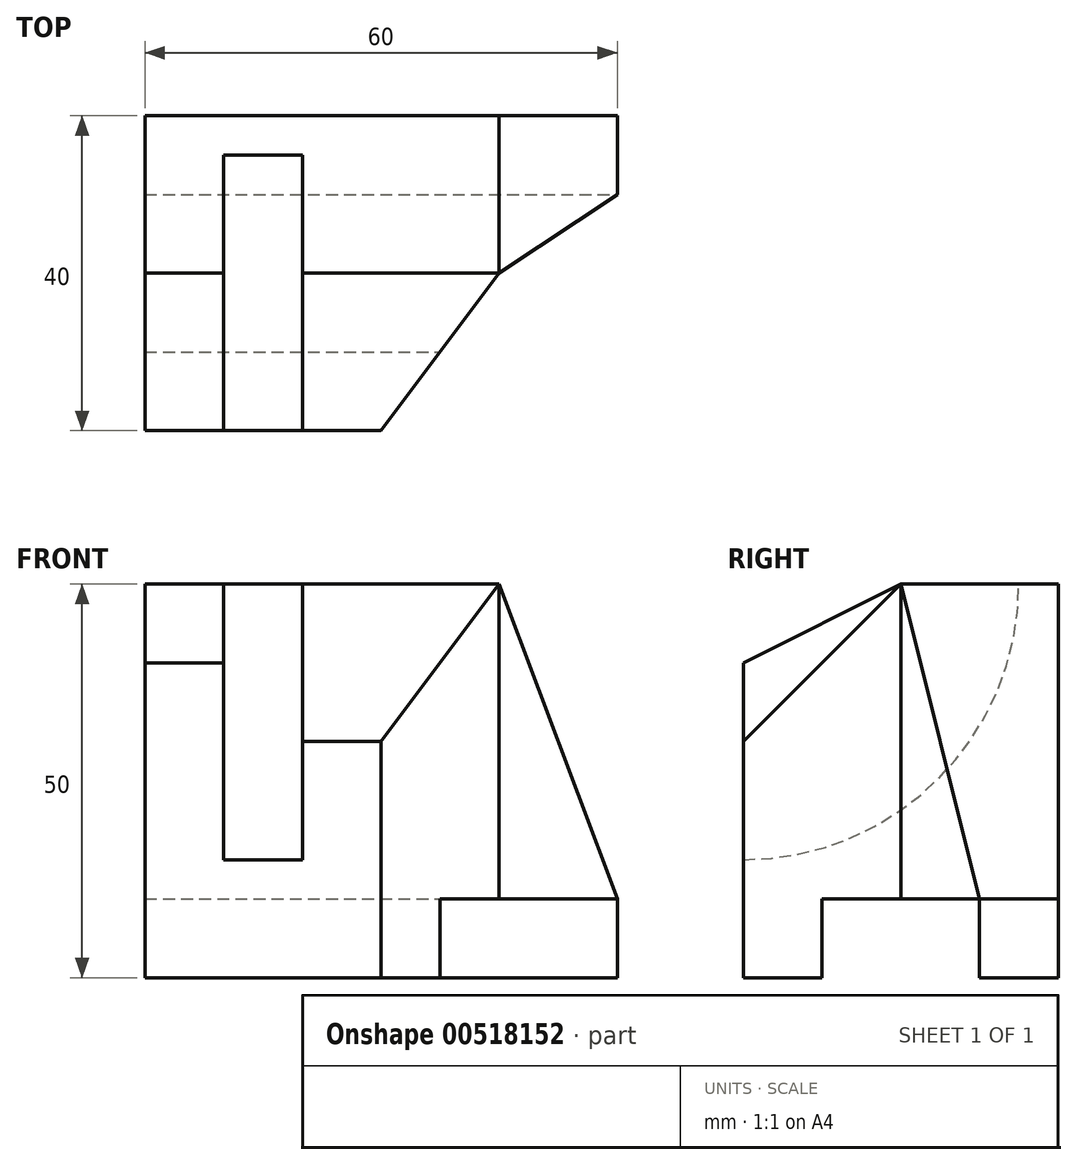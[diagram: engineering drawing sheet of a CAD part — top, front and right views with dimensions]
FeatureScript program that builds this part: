
annotation { "Feature Type Name" : "Feature", "Feature Type Description" : "" }
export const myFeature = defineFeature(function(context is Context, id is Id, definition is map)
    precondition{}
    {
        {
            var Q0;
            Q0=qCreatedBy(makeId("Top.planeOp"),FACE);
            var sketch = newSketch(context, id + "F0", { "sketchPlane" : qUnion([Q0])});
            skLineSegment(sketch, "E0.bottom", {"start": v(0, 0) * mm, "end": v(60, 0) * mm});
            skLineSegment(sketch, "E0.top", {"start": v(0, 40) * mm, "end": v(60, 40) * mm});
            skLineSegment(sketch, "E0.left", {"start": v(0, 0) * mm, "end": v(0, 40) * mm});
            skLineSegment(sketch, "E0.right", {"start": v(60, 0) * mm, "end": v(60, 40) * mm});
            skSolve(sketch);
        }
        {
            var Q0;
            Q0 = qSketchRegion(id + "F0", true);
            extrude(context, id + "F1", {"entities" : qUnion([Q0]), "depth" : 50 * mm, "offsetDistance" : 25 * mm});
        }
        {
            var Q0;
            Q0=makeQuery(id+"F1.opExtrude","SWEPT_FACE",FACE,{"disambiguationData":[OSD([sQuery(id+"F0.wireOp",EDGE,"E0.right")])]});
            var sketch = newSketch(context, id + "F2", { "sketchPlane" : qUnion([Q0])});
            skLineSegment(sketch, "E1.bottom", {"start": v(10, 0) * mm, "end": v(30, 0) * mm});
            skLineSegment(sketch, "E1.top", {"start": v(10, 10) * mm, "end": v(30, 10) * mm});
            skLineSegment(sketch, "E1.left", {"start": v(10, 0) * mm, "end": v(10, 10) * mm});
            skLineSegment(sketch, "E1.right", {"start": v(30, 0) * mm, "end": v(30, 10) * mm});
            skSolve(sketch);
        }
        {
            var Q0;
            Q0=makeQuery(id+"F2.imprint","IMPRINT",FACE,{"disambiguationData":[TD([[makeQuery(id+"F2.imprint","IMPRINT",EDGE,{"derivedFrom":sQuery(id+"F2.wireOp",EDGE,"E1.bottom")}),1.0]])]});
            extrude(context, id + "F3", {"entities" : qUnion([Q0]), "operationType" : NewBodyOperationType.REMOVE, "endBound" : BoundingType.THROUGH_ALL, "oppositeDirection" : true, "depth" : 25 * mm, "offsetDistance" : 25 * mm});
        }
        {
            var Q0;
            Q0=makeQuery(id+"F1.opExtrude","CAP_FACE",FACE,{"disambiguationData":[OSD([sQuery(id+"F0.wireOp",EDGE,"E0.bottom"),sQuery(id+"F0.wireOp",EDGE,"E0.top"),sQuery(id+"F0.wireOp",EDGE,"E0.left"),sQuery(id+"F0.wireOp",EDGE,"E0.right")])],"isStart":false});
            var sketch = newSketch(context, id + "F4", { "sketchPlane" : qUnion([Q0])});
            skLineSegment(sketch, "E2", {"start": v(0, 20) * mm, "end": v(10, 20) * mm});
            skLineSegment(sketch, "E3", {"start": v(10, 20) * mm, "end": v(20, 20) * mm});
            skLineSegment(sketch, "E4", {"start": v(20, 20) * mm, "end": v(45, 20) * mm});
            skLineSegment(sketch, "E5", {"start": v(45, 20) * mm, "end": v(30, 0) * mm});
            skLineSegment(sketch, "E6", {"start": v(60, 0) * mm, "end": v(60, 10) * mm});
            skLineSegment(sketch, "E7", {"start": v(60, 10) * mm, "end": v(60, 30) * mm});
            skLineSegment(sketch, "E8", {"start": v(45, 20) * mm, "end": v(60, 30) * mm});
            skSolve(sketch);
        }
        {
            var Q0;
            {var subQ1=sQuery(id+"F4.wireOp",EDGE,"E5");Q0=makeQuery(id+"F4.imprint","IMPRINT",FACE,{"disambiguationData":[TD([[makeQuery(id+"F4.imprint","IMPRINT",EDGE,{"derivedFrom":subQ1}),1.0]])]});}
            extrude(context, id + "F5", {"entities" : qUnion([Q0]), "operationType" : NewBodyOperationType.REMOVE, "endBound" : BoundingType.THROUGH_ALL, "oppositeDirection" : true, "depth" : 25 * mm, "offsetDistance" : 25 * mm});
        }
        {
            var Q0;
            Q0=makeQuery(id+"F1.opExtrude","CAP_FACE",FACE,{"disambiguationData":[OSD([sQuery(id+"F0.wireOp",EDGE,"E0.bottom"),sQuery(id+"F0.wireOp",EDGE,"E0.top"),sQuery(id+"F0.wireOp",EDGE,"E0.left"),sQuery(id+"F0.wireOp",EDGE,"E0.right")])],"isStart":false});
            var sketch = newSketch(context, id + "F6", { "sketchPlane" : qUnion([Q0])});
            skLineSegment(sketch, "E9", {"start": v(60, 20) * mm, "end": v(20, 20) * mm});
            skLineSegment(sketch, "E10", {"start": v(20, 20) * mm, "end": v(20, 0) * mm});
            skSolve(sketch);
        }
        {
            var Q0;
            Q0=makeQuery(id+"F1.opExtrude","SWEPT_FACE",FACE,{"disambiguationData":[OSD([sQuery(id+"F0.wireOp",EDGE,"E0.right")])]});
            var sketch = newSketch(context, id + "F7", { "sketchPlane" : qUnion([Q0])});
            skLineSegment(sketch, "E11", {"start": v(20, 50) * mm, "end": v(0, 30) * mm});
            skSolve(sketch);
        }
        {
            var Q0;
            {var subQ0=sQuery(id+"F6.wireOp",EDGE,"E9");Q0=makeQuery(id+"F6.imprint","IMPRINT",FACE,{"disambiguationData":[TD([[makeQuery(id+"F6.imprint","IMPRINT",EDGE,{"derivedFrom":subQ0}),1.0]])]});}
            var Q1;
            Q1=sQuery(id+"F7.wireOp",EDGE,"E11");
            sweep(context, id + "F8", {"operationType" : NewBodyOperationType.REMOVE, "profiles" : qUnion([Q0]), "path" : qUnion([Q1])});
        }
        {
            var Q0;
            Q0=makeQuery(id+"F1.opExtrude","CAP_FACE",FACE,{"disambiguationData":[OSD([sQuery(id+"F0.wireOp",EDGE,"E0.bottom"),sQuery(id+"F0.wireOp",EDGE,"E0.top"),sQuery(id+"F0.wireOp",EDGE,"E0.left"),sQuery(id+"F0.wireOp",EDGE,"E0.right")])],"isStart":false});
            var sketch = newSketch(context, id + "F9", { "sketchPlane" : qUnion([Q0])});
            skLineSegment(sketch, "E12.bottom", {"start": v(10, 0) * mm, "end": v(20, 0) * mm});
            skLineSegment(sketch, "E12.top", {"start": v(10, 35) * mm, "end": v(20, 35) * mm});
            skLineSegment(sketch, "E12.left", {"start": v(10, 0) * mm, "end": v(10, 35) * mm});
            skLineSegment(sketch, "E12.right", {"start": v(20, 0) * mm, "end": v(20, 35) * mm});
            skSolve(sketch);
        }
        {
            var Q0;
            Q0 = qSketchRegion(id + "F9", true);
            extrude(context, id + "F10", {"entities" : qUnion([Q0]), "operationType" : NewBodyOperationType.REMOVE, "oppositeDirection" : true, "depth" : 35 * mm, "offsetDistance" : 25 * mm});
        }
        {
            var Q0;
            Q0=makeQuery(id+"F10.boolean.opBoolean","COPY",EDGE,{"derivedFrom":makeQuery(id+"F10.opExtrude","CAP_EDGE",EDGE,{"disambiguationData":[OSD([sQuery(id+"F9.wireOp",EDGE,"E12.top")])],"isStart":false})});
            fillet(context, id + "F11", {"entities" : qUnion([Q0]), "radius" : 35 * mm, "tangentPropagation" : true, "allowEdgeOverflow" : false});
        }
        {
            var Q0;
            Q0=makeQuery(id+"F1.opExtrude","CAP_FACE",FACE,{"disambiguationData":[OSD([sQuery(id+"F0.wireOp",EDGE,"E0.bottom"),sQuery(id+"F0.wireOp",EDGE,"E0.top"),sQuery(id+"F0.wireOp",EDGE,"E0.left"),sQuery(id+"F0.wireOp",EDGE,"E0.right")])],"isStart":false});
            var sketch = newSketch(context, id + "F12", { "sketchPlane" : qUnion([Q0])});
            skLineSegment(sketch, "E13", {"start": v(0, 20) * mm, "end": v(10, 20) * mm});
            skSolve(sketch);
        }
        {
            var Q0;
            Q0=makeQuery(id+"F1.opExtrude","SWEPT_FACE",FACE,{"disambiguationData":[OSD([sQuery(id+"F0.wireOp",EDGE,"E0.left")])]});
            var sketch = newSketch(context, id + "F13", { "sketchPlane" : qUnion([Q0])});
            skLineSegment(sketch, "E14", {"start": v(0, 40) * mm, "end": v(-20, 50) * mm});
            skSolve(sketch);
        }
        {
            var Q0;
            {var subQ0=sQuery(id+"F12.wireOp",EDGE,"E13");Q0=makeQuery(id+"F12.imprint","IMPRINT",FACE,{"disambiguationData":[TD([[makeQuery(id+"F12.imprint","IMPRINT",EDGE,{"derivedFrom":subQ0}),-1.0]])]});}
            var Q1;
            Q1=sQuery(id+"F13.wireOp",EDGE,"E14");
            sweep(context, id + "F14", {"operationType" : NewBodyOperationType.REMOVE, "profiles" : qUnion([Q0]), "path" : qUnion([Q1])});
        }
        {
            var Q0;
            Q0=makeQuery(id+"F1.opExtrude","SWEPT_FACE",FACE,{"disambiguationData":[OSD([sQuery(id+"F0.wireOp",EDGE,"E0.top")])]});
            var sketch = newSketch(context, id + "F15", { "sketchPlane" : qUnion([Q0])});
            skLineSegment(sketch, "E15", {"start": v(0, 50) * mm, "end": v(-45, 50) * mm});
            skLineSegment(sketch, "E16", {"start": v(-45, 50) * mm, "end": v(-60, 10) * mm});
            skSolve(sketch);
        }
        {
            var Q0;
            {var subQ0=sQuery(id+"F15.wireOp",EDGE,"E16");Q0=makeQuery(id+"F15.imprint","IMPRINT",FACE,{"disambiguationData":[TD([[makeQuery(id+"F15.imprint","IMPRINT",EDGE,{"derivedFrom":subQ0}),-1.0]])]});}
            extrude(context, id + "F16", {"entities" : qUnion([Q0]), "operationType" : NewBodyOperationType.REMOVE, "endBound" : BoundingType.THROUGH_ALL, "oppositeDirection" : true, "depth" : 25 * mm, "offsetDistance" : 25 * mm});
        }
    });
